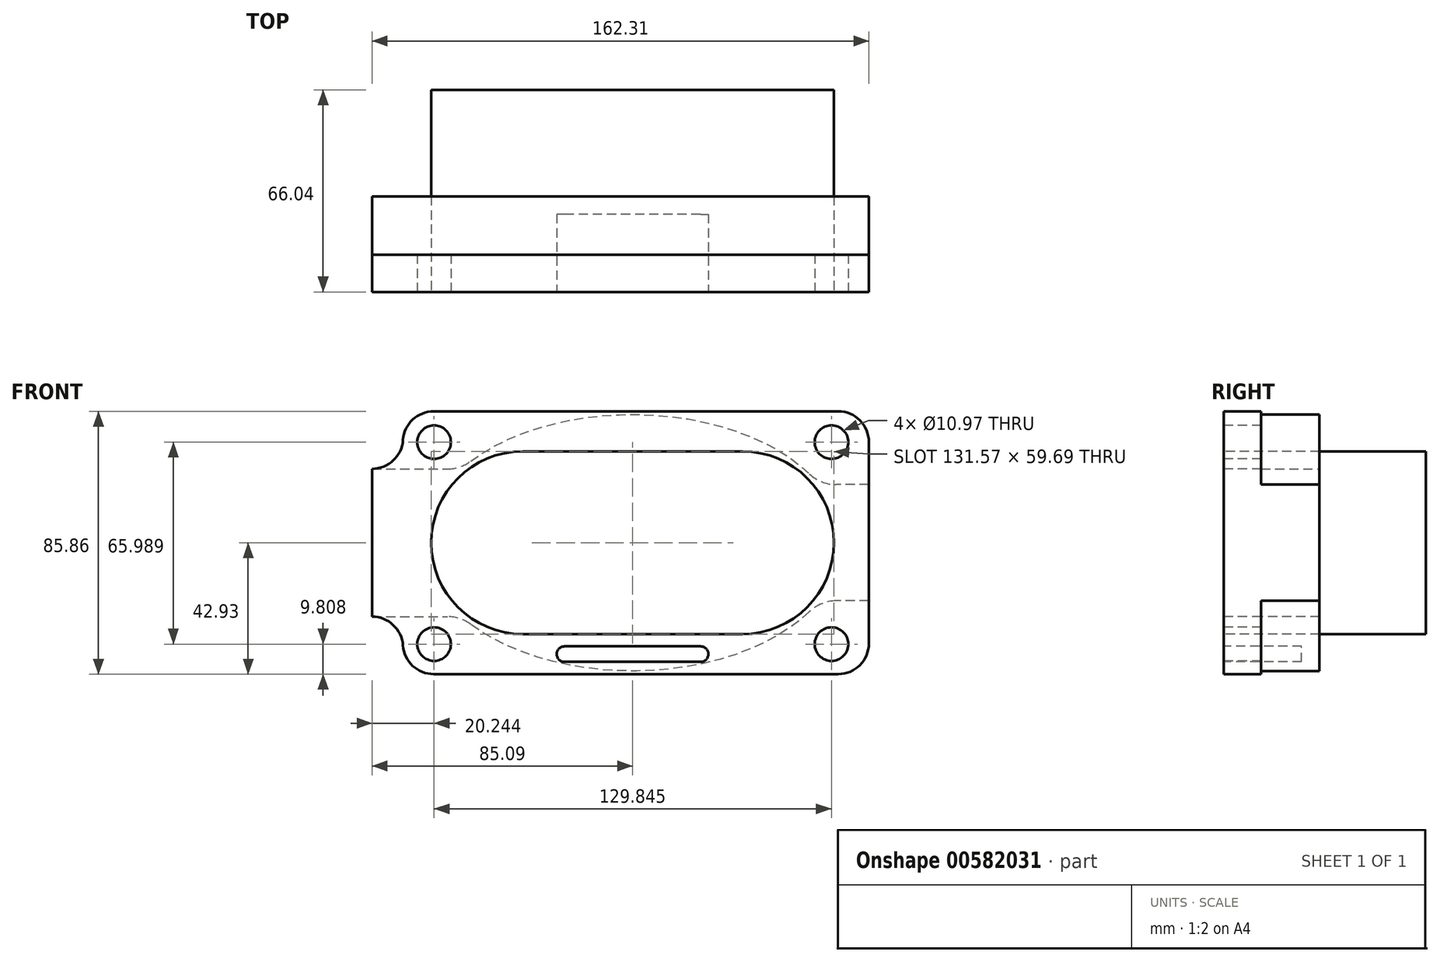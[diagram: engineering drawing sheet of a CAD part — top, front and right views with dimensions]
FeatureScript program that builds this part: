
annotation { "Feature Type Name" : "Feature", "Feature Type Description" : "" }
export const myFeature = defineFeature(function(context is Context, id is Id, definition is map)
    precondition{}
    {
        {
            var Q0;
            Q0=qCreatedBy(makeId("Front.planeOp"),FACE);
            var sketch = newSketch(context, id + "F0", { "sketchPlane" : qUnion([Q0])});
            skLineSegment(sketch, "E0", {"start": v(-35.94, 0) * mm, "end": v(35.94, 0) * mm, "construction": true});
            skArc(sketch, "E1.0.startCap", {"start": v(-35.94, -29.85) * mm, "mid": v(-65.79, 0) * mm, "end": v(-35.94, 29.85) * mm});
            skArc(sketch, "E1.0.endCap", {"start": v(35.94, 29.85) * mm, "mid": v(65.79, 0) * mm, "end": v(35.94, -29.85) * mm});
            skLineSegment(sketch, "E1.0.left", {"start": v(-35.94, 29.85) * mm, "end": v(35.94, 29.85) * mm});
            skLineSegment(sketch, "E1.0.right", {"start": v(-35.94, -29.85) * mm, "end": v(35.94, -29.85) * mm});
            skPoint(sketch, "E2", {"position": v(-65.79, 0) * mm});
            skPoint(sketch, "E3", {"position": v(65.79, 0) * mm});
            skLineSegment(sketch, "E4", {"start": v(-85.1, 24.13) * mm, "end": v(-85.09, -24.13) * mm});
            skLineSegment(sketch, "E5", {"start": v(-85.1, -24.13) * mm, "end": v(-75.03, -24.13) * mm});
            skLineSegment(sketch, "E6", {"start": v(-75.03, -24.13) * mm, "end": v(-75.03, -42.93) * mm});
            skPoint(sketch, "E7", {"position": v(-85.1, 0) * mm});
            skLineSegment(sketch, "E8", {"start": v(-75.03, -42.93) * mm, "end": v(77.22, -42.93) * mm});
            skLineSegment(sketch, "E9", {"start": v(-85.1, 24.13) * mm, "end": v(-75.03, 24.13) * mm});
            skLineSegment(sketch, "E10", {"start": v(-75.03, 24.13) * mm, "end": v(-75.03, 42.93) * mm});
            skLineSegment(sketch, "E11", {"start": v(-75.03, 42.93) * mm, "end": v(77.22, 42.93) * mm});
            skLineSegment(sketch, "E12", {"start": v(77.22, 42.93) * mm, "end": v(77.22, -42.93) * mm});
            skCircle(sketch, "E13", {"center": v(-64.85, 32.87) * mm, "radius": 5.49 * mm});
            skCircle(sketch, "E14", {"center": v(65, 32.87) * mm, "radius": 5.49 * mm});
            skLineSegment(sketch, "E15", {"start": v(-64.85, 32.87) * mm, "end": v(65, 32.87) * mm, "construction": true});
            skPoint(sketch, "E16", {"position": v(-70.33, 32.87) * mm});
            skPoint(sketch, "E17", {"position": v(-59.36, 32.87) * mm});
            skPoint(sketch, "E18", {"position": v(70.48, 32.87) * mm});
            skPoint(sketch, "E19", {"position": v(59.51, 32.87) * mm});
            skPoint(sketch, "E20", {"position": v(-64.85, 38.35) * mm});
            skLineSegment(sketch, "E21", {"start": v(-64.85, -33.12) * mm, "end": v(65, -33.12) * mm, "construction": true});
            skCircle(sketch, "E22", {"center": v(-64.85, -33.12) * mm, "radius": 5.49 * mm});
            skCircle(sketch, "E23", {"center": v(65, -33.12) * mm, "radius": 5.49 * mm});
            skPoint(sketch, "E24", {"position": v(-64.85, -38.6) * mm});
            skPoint(sketch, "E25", {"position": v(70.48, -33.12) * mm});
            skPoint(sketch, "E26", {"position": v(-59.36, -33.12) * mm});
            skPoint(sketch, "E27", {"position": v(59.51, -33.12) * mm});
            skSolve(sketch);
        }
        {
            var Q0;
            Q0 = qSketchRegion(id + "F0", true);
            extrude(context, id + "F1", {"entities" : qUnion([Q0]), "oppositeDirection" : true, "depth" : 12.2 * mm, "offsetDistance" : 25.4 * mm});
        }
        {
            var Q0;
            Q0=makeQuery(id+"F1.opExtrude","CAP_FACE",FACE,{"disambiguationData":[OSD([sQuery(id+"F0.wireOp",EDGE,"E1.0.startCap"),sQuery(id+"F0.wireOp",EDGE,"E1.0.endCap"),sQuery(id+"F0.wireOp",EDGE,"E1.0.left"),sQuery(id+"F0.wireOp",EDGE,"E1.0.right"),sQuery(id+"F0.wireOp",EDGE,"E4"),sQuery(id+"F0.wireOp",EDGE,"E5"),sQuery(id+"F0.wireOp",EDGE,"E6"),sQuery(id+"F0.wireOp",EDGE,"E8"),sQuery(id+"F0.wireOp",EDGE,"E9"),sQuery(id+"F0.wireOp",EDGE,"E10"),sQuery(id+"F0.wireOp",EDGE,"E11"),sQuery(id+"F0.wireOp",EDGE,"E12"),sQuery(id+"F0.wireOp",EDGE,"E13"),sQuery(id+"F0.wireOp",EDGE,"E14"),sQuery(id+"F0.wireOp",EDGE,"E22"),sQuery(id+"F0.wireOp",EDGE,"E23")])],"isStart":false});
            var sketch = newSketch(context, id + "F2", { "sketchPlane" : qUnion([Q0])});
            skEllipse(sketch, "E28", {"center": v(0, 0) * mm, "majorRadius": 68.52 * mm, "minorRadius": 41.91 * mm, "majorAxis": v(-1, 0)});
            skPoint(sketch, "E29", {"position": v(0, -41.91) * mm});
            skPoint(sketch, "E30", {"position": v(0, 41.91) * mm});
            skPoint(sketch, "E31", {"position": v(68.52, 0) * mm});
            skPoint(sketch, "E32", {"position": v(-68.52, 0) * mm});
            skLineSegment(sketch, "E33", {"start": v(-77.22, -18.99) * mm, "end": v(-77.22, 18.99) * mm});
            skPoint(sketch, "E34", {"position": v(-77.22, 0) * mm});
            skLineSegment(sketch, "E35", {"start": v(-77.22, -18.99) * mm, "end": v(-61.08, -18.99) * mm});
            skLineSegment(sketch, "E36", {"start": v(-77.22, 18.99) * mm, "end": v(-61.08, 18.99) * mm});
            skLineSegment(sketch, "E37", {"start": v(85.1, 24.13) * mm, "end": v(56.02, 24.13) * mm});
            skLineSegment(sketch, "E38", {"start": v(85.1, 24.13) * mm, "end": v(85.1, -24.13) * mm});
            skLineSegment(sketch, "E39", {"start": v(85.1, -24.13) * mm, "end": v(56.02, -24.13) * mm});
            skArc(sketch, "E40.0", {"start": v(35.94, -29.85) * mm, "mid": v(65.79, 0) * mm, "end": v(35.94, 29.85) * mm});
            skLineSegment(sketch, "E40.1", {"start": v(35.94, -29.85) * mm, "end": v(-35.94, -29.85) * mm});
            skArc(sketch, "E40.2", {"start": v(-35.94, 29.85) * mm, "mid": v(-65.79, 0) * mm, "end": v(-35.94, -29.85) * mm});
            skLineSegment(sketch, "E40.3", {"start": v(35.94, 29.85) * mm, "end": v(-35.94, 29.85) * mm});
            skSolve(sketch);
        }
        {
            var Q0;
            Q0 = qSketchRegion(id + "F2", true);
            extrude(context, id + "F3", {"entities" : qUnion([Q0]), "operationType" : NewBodyOperationType.ADD, "depth" : 19.05 * mm, "offsetDistance" : 25.4 * mm});
        }
        {
            var Q0;
            Q0=makeQuery(id+"F3.opExtrude","CAP_FACE",FACE,{"disambiguationData":[OSD([sQuery(id+"F2.wireOp",EDGE,"E28"),sQuery(id+"F2.wireOp",EDGE,"E33"),sQuery(id+"F2.wireOp",EDGE,"E35"),sQuery(id+"F2.wireOp",EDGE,"E36"),sQuery(id+"F2.wireOp",EDGE,"E37"),sQuery(id+"F2.wireOp",EDGE,"E38"),sQuery(id+"F2.wireOp",EDGE,"E39"),sQuery(id+"F2.wireOp",EDGE,"E40.0"),sQuery(id+"F2.wireOp",EDGE,"E40.1"),sQuery(id+"F2.wireOp",EDGE,"E40.2"),sQuery(id+"F2.wireOp",EDGE,"E40.3")])],"isStart":false});
            var sketch = newSketch(context, id + "F4", { "sketchPlane" : qUnion([Q0])});
            skEllipse(sketch, "E41.0", {"center": v(0, 0) * mm, "majorRadius": 68.52 * mm, "minorRadius": 41.91 * mm, "majorAxis": v(-1, 0)});
            skSolve(sketch);
        }
        {
            var Q0;
            Q0=makeQuery(id+"F4.imprint","IMPRINT",FACE,{"disambiguationData":[TD([[makeQuery(id+"F4.imprint","IMPRINT",EDGE,{"derivedFrom":makeQuery(id+"F3.opExtrude","CAP_EDGE",EDGE,{"disambiguationData":[OSD([sQuery(id+"F2.wireOp",EDGE,"E40.0")])],"isStart":false})}),-1.0]])]});
            extrude(context, id + "F5", {"entities" : qUnion([Q0]), "operationType" : NewBodyOperationType.ADD, "depth" : 34.8 * mm, "offsetDistance" : 25.4 * mm});
        }
        {
            var Q0;
            Q0=makeQuery(id+"F1.opExtrude","SWEPT_EDGE",EDGE,{"disambiguationData":[OSD([sQuery(id+"F0.wireOp",EDGE,"E10"),sQuery(id+"F0.wireOp",EDGE,"E11")])]});
            var Q1;
            Q1=makeQuery(id+"F1.opExtrude","SWEPT_EDGE",EDGE,{"disambiguationData":[OSD([sQuery(id+"F0.wireOp",EDGE,"E11"),sQuery(id+"F0.wireOp",EDGE,"E12")])]});
            var Q2;
            Q2=makeQuery(id+"F1.opExtrude","SWEPT_EDGE",EDGE,{"disambiguationData":[OSD([sQuery(id+"F0.wireOp",EDGE,"E8"),sQuery(id+"F0.wireOp",EDGE,"E12")])]});
            var Q3;
            Q3=makeQuery(id+"F1.opExtrude","SWEPT_EDGE",EDGE,{"disambiguationData":[OSD([sQuery(id+"F0.wireOp",EDGE,"E6"),sQuery(id+"F0.wireOp",EDGE,"E8")])]});
            fillet(context, id + "F6", {"entities" : qUnion([Q0, Q1, Q2, Q3]), "radius" : 10.03 * mm, "tangentPropagation" : true, "allowEdgeOverflow" : false});
        }
        {
            var Q0;
            Q0=makeQuery(id+"F1.opExtrude","SWEPT_EDGE",EDGE,{"disambiguationData":[OSD([sQuery(id+"F0.wireOp",EDGE,"E5"),sQuery(id+"F0.wireOp",EDGE,"E6")])]});
            var Q1;
            Q1=makeQuery(id+"F1.opExtrude","SWEPT_EDGE",EDGE,{"disambiguationData":[OSD([sQuery(id+"F0.wireOp",EDGE,"E9"),sQuery(id+"F0.wireOp",EDGE,"E10")])]});
            fillet(context, id + "F7", {"entities" : qUnion([Q0, Q1]), "radius" : 10.16 * mm, "tangentPropagation" : true, "allowEdgeOverflow" : false});
        }
        {
            var Q0;
            Q0=makeQuery(id+"F3.opExtrude","SWEPT_EDGE",EDGE,{"disambiguationData":[OSD([sQuery(id+"F2.wireOp",EDGE,"E28"),sQuery(id+"F2.wireOp",EDGE,"E37")])]});
            var Q1;
            Q1=makeQuery(id+"F3.opExtrude","SWEPT_EDGE",EDGE,{"disambiguationData":[OSD([sQuery(id+"F2.wireOp",EDGE,"E28"),sQuery(id+"F2.wireOp",EDGE,"E36")])]});
            var Q2;
            Q2=makeQuery(id+"F3.opExtrude","SWEPT_EDGE",EDGE,{"disambiguationData":[OSD([sQuery(id+"F2.wireOp",EDGE,"E28"),sQuery(id+"F2.wireOp",EDGE,"E35")])]});
            var Q3;
            Q3=makeQuery(id+"F3.opExtrude","SWEPT_EDGE",EDGE,{"disambiguationData":[OSD([sQuery(id+"F2.wireOp",EDGE,"E28"),sQuery(id+"F2.wireOp",EDGE,"E39")])]});
            fillet(context, id + "F8", {"entities" : qUnion([Q0, Q1, Q2, Q3]), "radius" : 12.7 * mm, "tangentPropagation" : true, "allowEdgeOverflow" : false});
        }
        {
            var Q0;
            Q0=makeQuery(id+"F1.opExtrude","CAP_FACE",FACE,{"disambiguationData":[OSD([sQuery(id+"F0.wireOp",EDGE,"E1.0.startCap"),sQuery(id+"F0.wireOp",EDGE,"E1.0.endCap"),sQuery(id+"F0.wireOp",EDGE,"E1.0.left"),sQuery(id+"F0.wireOp",EDGE,"E1.0.right"),sQuery(id+"F0.wireOp",EDGE,"E4"),sQuery(id+"F0.wireOp",EDGE,"E5"),sQuery(id+"F0.wireOp",EDGE,"E6"),sQuery(id+"F0.wireOp",EDGE,"E8"),sQuery(id+"F0.wireOp",EDGE,"E9"),sQuery(id+"F0.wireOp",EDGE,"E10"),sQuery(id+"F0.wireOp",EDGE,"E11"),sQuery(id+"F0.wireOp",EDGE,"E12"),sQuery(id+"F0.wireOp",EDGE,"E13"),sQuery(id+"F0.wireOp",EDGE,"E14"),sQuery(id+"F0.wireOp",EDGE,"E22"),sQuery(id+"F0.wireOp",EDGE,"E23")])],"isStart":true});
            var sketch = newSketch(context, id + "F9", { "sketchPlane" : qUnion([Q0])});
            skLineSegment(sketch, "E42", {"start": v(22.23, -36.4) * mm, "end": v(-22.22, -36.4) * mm, "construction": true});
            skArc(sketch, "E43.0.startCap", {"start": v(22.23, -33.86) * mm, "mid": v(24.77, -36.4) * mm, "end": v(22.23, -38.94) * mm});
            skArc(sketch, "E43.0.endCap", {"start": v(-22.23, -38.94) * mm, "mid": v(-24.77, -36.4) * mm, "end": v(-22.23, -33.86) * mm});
            skLineSegment(sketch, "E43.0.left", {"start": v(22.23, -38.94) * mm, "end": v(-22.23, -38.94) * mm});
            skLineSegment(sketch, "E43.0.right", {"start": v(22.23, -33.86) * mm, "end": v(-22.23, -33.86) * mm});
            skPoint(sketch, "E44", {"position": v(0, -36.4) * mm});
            skPoint(sketch, "E45", {"position": v(24.77, -36.4) * mm});
            skPoint(sketch, "E46", {"position": v(-24.77, -36.4) * mm});
            skSolve(sketch);
        }
        {
            var Q0;
            Q0 = qSketchRegion(id + "F9", true);
            extrude(context, id + "F10", {"entities" : qUnion([Q0]), "operationType" : NewBodyOperationType.REMOVE, "oppositeDirection" : true, "depth" : 25.4 * mm, "offsetDistance" : 25.4 * mm});
        }
    });
